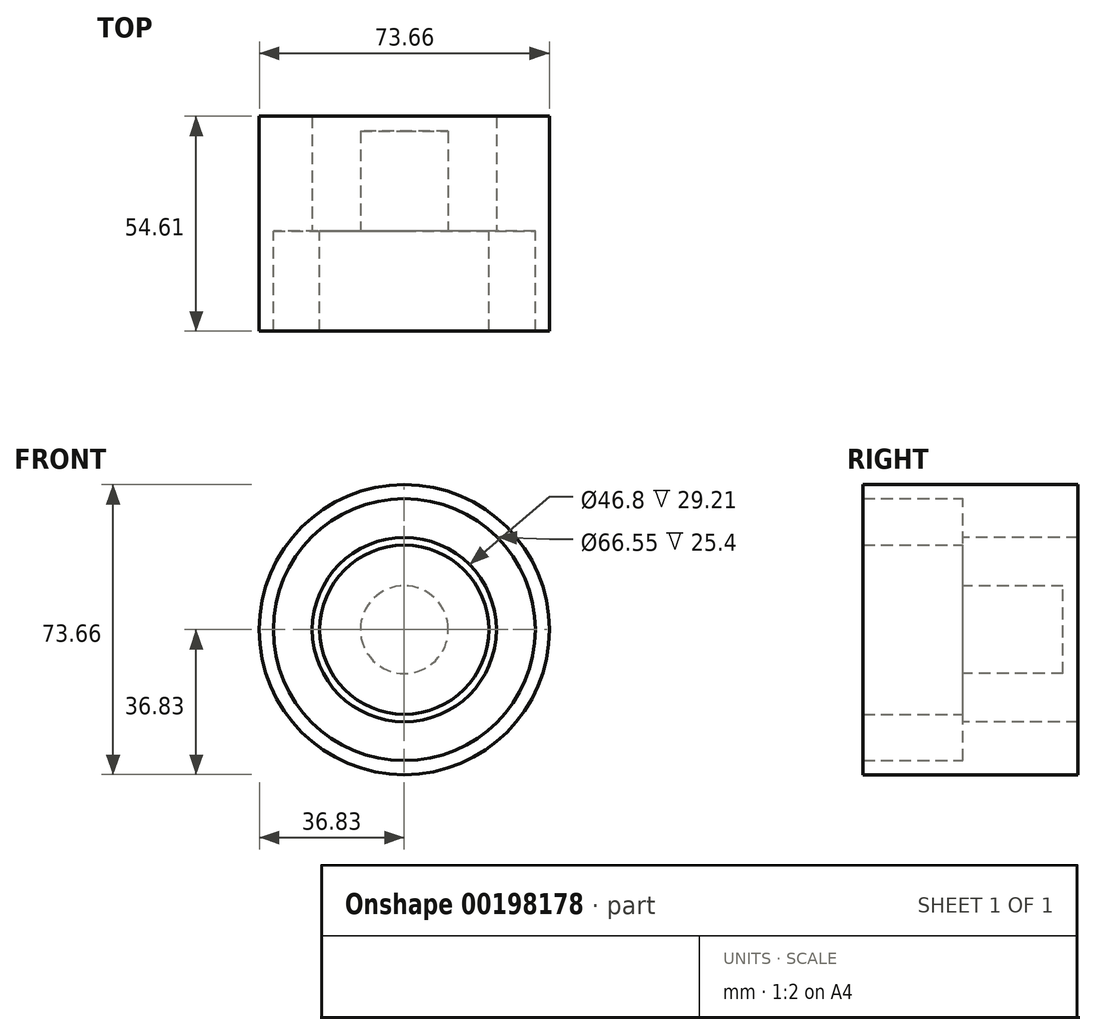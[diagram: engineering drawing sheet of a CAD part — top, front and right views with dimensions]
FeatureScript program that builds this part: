
annotation { "Feature Type Name" : "Feature", "Feature Type Description" : "" }
export const myFeature = defineFeature(function(context is Context, id is Id, definition is map)
    precondition{}
    {
        {
            var Q0;
            Q0=qCreatedBy(makeId("Front.planeOp"),FACE);
            var sketch = newSketch(context, id + "F0", { "sketchPlane" : qUnion([Q0])});
            skCircle(sketch, "E0", {"center": v(0, 0) * mm, "radius": 32.53 * mm, "construction": true});
            skCircle(sketch, "E1", {"center": v(0, 0) * mm, "radius": 26.76 * mm, "construction": true});
            skCircle(sketch, "E2", {"center": v(0, 0) * mm, "radius": 13.7 * mm, "construction": true});
            skCircle(sketch, "E3", {"center": v(0, 0) * mm, "radius": 17.52 * mm, "construction": true});
            skCircle(sketch, "E4", {"center": v(0, 0) * mm, "radius": 21.48 * mm});
            skCircle(sketch, "E5.0", {"center": v(0, 0) * mm, "radius": 11.17 * mm});
            skSolve(sketch);
        }
        {
            var Q0;
            Q0=makeQuery(id+"F0.imprint","IMPRINT",FACE,{"disambiguationData":[TD([[makeQuery(id+"F0.imprint","IMPRINT",EDGE,{"derivedFrom":sQuery(id+"F0.wireOp",EDGE,"E5.0")}),1.0]])]});
            extrude(context, id + "F1", {"entities" : qUnion([Q0]), "oppositeDirection" : true, "depth" : 25.4 * mm});
        }
        {
            var Q0;
            Q0 = qSketchRegion(id + "F0", true);
            var Q1;
            Q1=makeQuery(id+"F1.opExtrude","CAP_FACE",FACE,{"disambiguationData":[OSD([sQuery(id+"F0.wireOp",EDGE,"E5.0")])],"isStart":true});
            extrude(context, id + "F2", {"entities" : qUnion([Q0, Q1]), "operationType" : NewBodyOperationType.ADD, "depth" : 25.4 * mm});
        }
        {
            var Q0;
            Q0=qCreatedBy(makeId("Front.planeOp"),FACE);
            var sketch = newSketch(context, id + "F3", { "sketchPlane" : qUnion([Q0])});
            skCircle(sketch, "E6", {"center": v(0, 0) * mm, "radius": 36.83 * mm});
            skCircle(sketch, "E7", {"center": v(0, 0) * mm, "radius": 23.4 * mm});
            skSolve(sketch);
        }
        {
            var Q0;
            Q0 = qSketchRegion(id + "F3", true);
            extrude(context, id + "F4", {"entities" : qUnion([Q0]), "oppositeDirection" : true, "depth" : 29.2 * mm});
        }
        {
            var Q0;
            Q0=makeQuery(id+"F4.opExtrude","CAP_FACE",FACE,{"disambiguationData":[OSD([sQuery(id+"F3.wireOp",EDGE,"E6"),sQuery(id+"F3.wireOp",EDGE,"E7")])],"isStart":true});
            var sketch = newSketch(context, id + "F5", { "sketchPlane" : qUnion([Q0])});
            skCircle(sketch, "E8", {"center": v(0, 0) * mm, "radius": 33.27 * mm});
            skCircle(sketch, "E9.0", {"center": v(0, 0) * mm, "radius": 36.83 * mm});
            skSolve(sketch);
        }
        {
            var Q0;
            Q0 = qSketchRegion(id + "F5", true);
            extrude(context, id + "F6", {"entities" : qUnion([Q0]), "operationType" : NewBodyOperationType.ADD, "depth" : 25.4 * mm});
        }
    });
